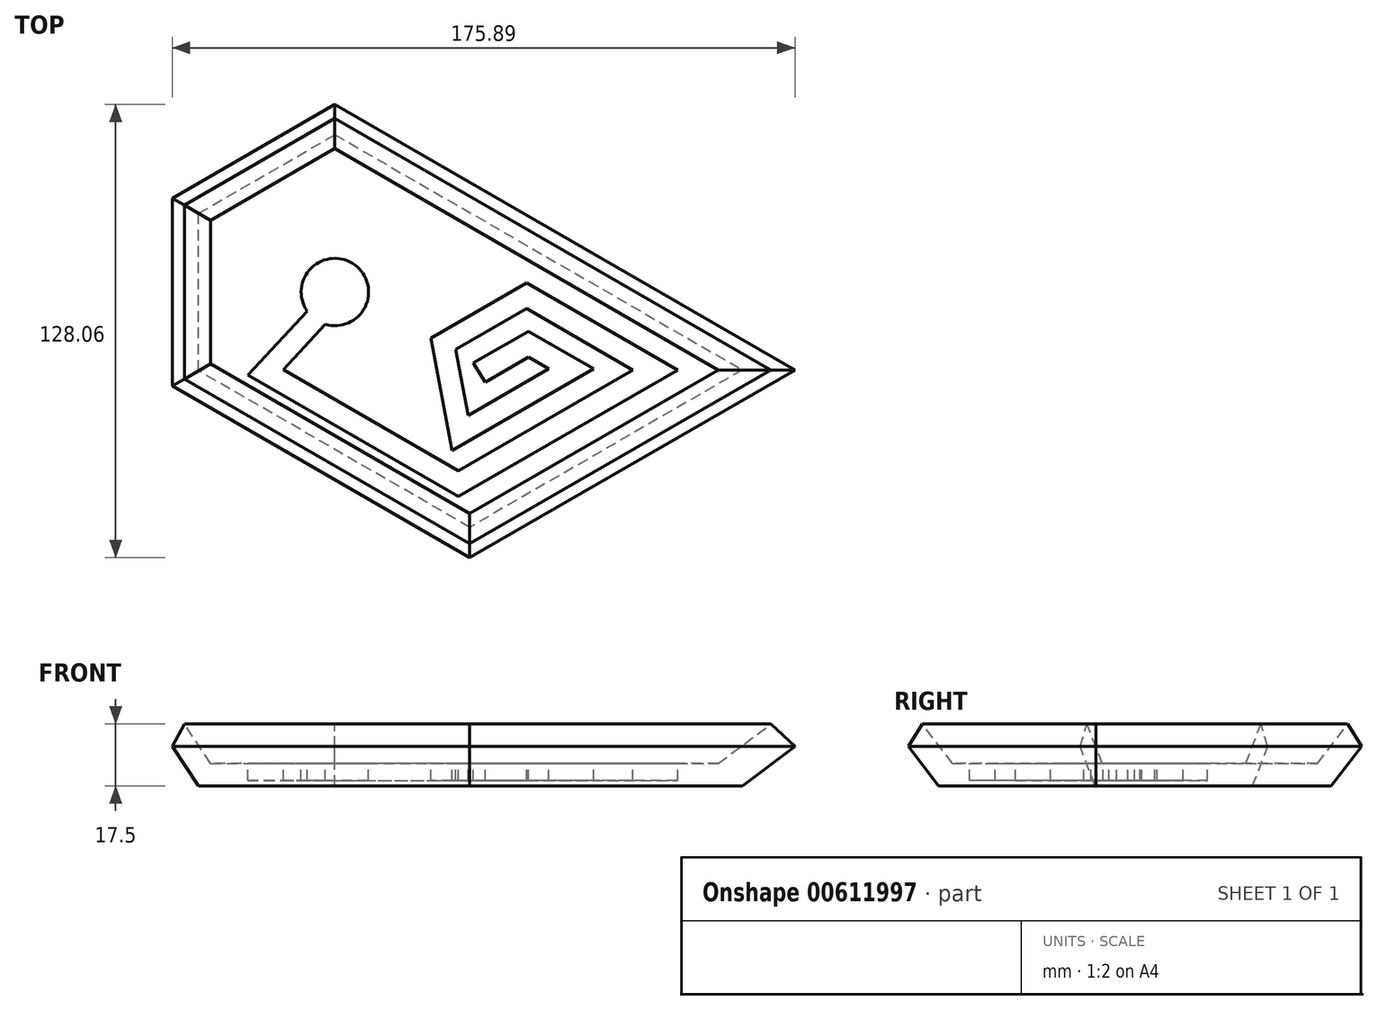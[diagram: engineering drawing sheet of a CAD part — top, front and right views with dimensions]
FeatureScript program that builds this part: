
annotation { "Feature Type Name" : "Feature", "Feature Type Description" : "" }
export const myFeature = defineFeature(function(context is Context, id is Id, definition is map)
    precondition{}
    {
        {
            var Q0;
            Q0=qCreatedBy(makeId("Top.planeOp"),FACE);
            var sketch = newSketch(context, id + "F0", { "sketchPlane" : qUnion([Q0])});
            skCircle(sketch, "E0.cCircle", {"center": v(0, 0) * mm, "radius": 38.5 * mm, "construction": true});
            skLineSegment(sketch, "E0.0", {"start": v(38.5, 22.22) * mm, "end": v(38.5, -22.22) * mm, "construction": true});
            skLineSegment(sketch, "E0.1", {"start": v(38.5, -22.23) * mm, "end": v(0, -44.45) * mm, "construction": true});
            skLineSegment(sketch, "E0.2", {"start": v(0, -44.45) * mm, "end": v(-38.5, -22.23) * mm});
            skLineSegment(sketch, "E0.3", {"start": v(-38.5, -22.22) * mm, "end": v(-38.5, 22.22) * mm});
            skLineSegment(sketch, "E0.4", {"start": v(-38.5, 22.22) * mm, "end": v(0, 44.45) * mm});
            skLineSegment(sketch, "E0.5", {"start": v(0, 44.45) * mm, "end": v(38.5, 22.23) * mm});
            skPoint(sketch, "E0.0.midPoint", {"position": v(38.5, 0) * mm});
            skLineSegment(sketch, "E1", {"start": v(38.5, 22.23) * mm, "end": v(115.09, -22) * mm});
            skLineSegment(sketch, "E2", {"start": v(115.09, -22) * mm, "end": v(38.1, -66.45) * mm});
            skLineSegment(sketch, "E3", {"start": v(38.1, -66.45) * mm, "end": v(0, -44.45) * mm});
            skSolve(sketch);
        }
        {
            var Q0;
            Q0=qCreatedBy(makeId("Top.planeOp"),FACE);
            cPlane(context, id + "F1", {"entities" : qUnion([Q0]), "cplaneType" : CPlaneType.OFFSET, "offset" : 19.05 * mm, "width" : 152.4 * mm, "height" : 152.4 * mm});
        }
        {
            var Q0;
            Q0=qCreatedBy(id+"F1.planeOp",FACE);
            var sketch = newSketch(context, id + "F2", { "sketchPlane" : qUnion([Q0])});
            skLineSegment(sketch, "E4.0", {"start": v(-51.2, -29.56) * mm, "end": v(-51.2, 29.56) * mm});
            skLineSegment(sketch, "E4.1", {"start": v(14.46, -67.46) * mm, "end": v(-51.2, -29.56) * mm});
            skLineSegment(sketch, "E4.2", {"start": v(-51.2, 29.56) * mm, "end": v(0, 59.11) * mm});
            skLineSegment(sketch, "E4.3", {"start": v(38.1, -81.11) * mm, "end": v(14.46, -67.46) * mm});
            skLineSegment(sketch, "E4.4", {"start": v(140.49, -22) * mm, "end": v(38.1, -81.11) * mm});
            skLineSegment(sketch, "E4.5", {"start": v(0, 59.11) * mm, "end": v(65.65, 21.2) * mm});
            skLineSegment(sketch, "E4.8", {"start": v(65.65, 21.2) * mm, "end": v(140.49, -22) * mm});
            skSolve(sketch);
        }
        {
            var Q0;
            Q0=makeQuery(id+"F0.imprint","IMPRINT",FACE,{"disambiguationData":[TD([[makeQuery(id+"F0.imprint","IMPRINT",EDGE,{"derivedFrom":sQuery(id+"F0.wireOp",EDGE,"E0.2")}),-1.0]])]});
            var Q1;
            Q1=makeQuery(id+"F2.imprint","IMPRINT",FACE,{"disambiguationData":[TD([[makeQuery(id+"F2.imprint","IMPRINT",EDGE,{"derivedFrom":sQuery(id+"F2.wireOp",EDGE,"E4.0")}),-1.0]])]});
            loft(context, id + "F3", {"sheetProfilesArray" : [{ "sheetProfileEntities" : qUnion([Q0]) }, { "sheetProfileEntities" : qUnion([Q1]) }]});
        }
        {
            var Q0;
            Q0=makeQuery(id+"F3.opLoft","CAP_FACE",FACE,{"disambiguationData":[OSD([makeQuery(id+"F2.imprint","IMPRINT",FACE,{"disambiguationData":[TD([[makeQuery(id+"F2.imprint","IMPRINT",EDGE,{"derivedFrom":sQuery(id+"F2.wireOp",EDGE,"E4.0")}),-1.0]])]})])],"isStart":true});
            shell(context, id + "F4", {"entities" : qUnion([Q0]), "thickness" : 6.35 * mm});
        }
        {
            var Q0;
            Q0=makeQuery(id+"F4.opShell","OFFSET_FACE",FACE,{"disambiguationData":[OSD([makeQuery(id+"F0.imprint","IMPRINT",FACE,{"disambiguationData":[TD([[makeQuery(id+"F0.imprint","IMPRINT",EDGE,{"derivedFrom":sQuery(id+"F0.wireOp",EDGE,"E0.2")}),-1.0]])]})])]});
            var sketch = newSketch(context, id + "F5", { "sketchPlane" : qUnion([Q0])});
            skCircle(sketch, "E5", {"center": v(0, 0) * mm, "radius": 9.53 * mm});
            skSolve(sketch);
        }
        {
            var Q0;
            Q0 = qSketchRegion(id + "F5", true);
            extrude(context, id + "F6", {"entities" : qUnion([Q0]), "operationType" : NewBodyOperationType.REMOVE, "oppositeDirection" : true, "depth" : 4.76 * mm, "offsetDistance" : 25.4 * mm});
        }
        {
            var Q0;
            Q0=makeQuery(id+"F4.opShell","OFFSET_FACE",FACE,{"disambiguationData":[OSD([makeQuery(id+"F0.imprint","IMPRINT",FACE,{"disambiguationData":[TD([[makeQuery(id+"F0.imprint","IMPRINT",EDGE,{"derivedFrom":sQuery(id+"F0.wireOp",EDGE,"E0.2")}),-1.0]])]})])]});
            var sketch = newSketch(context, id + "F7", { "sketchPlane" : qUnion([Q0])});
            skLineSegment(sketch, "E6", {"start": v(34.83, -50.45) * mm, "end": v(84.1, -22) * mm});
            skLineSegment(sketch, "E7", {"start": v(84.1, -22) * mm, "end": v(54.17, -4.71) * mm});
            skLineSegment(sketch, "E8", {"start": v(54.17, -4.71) * mm, "end": v(34.17, -16.26) * mm});
            skLineSegment(sketch, "E9", {"start": v(34.17, -16.26) * mm, "end": v(37.68, -34.83) * mm});
            skLineSegment(sketch, "E10", {"start": v(37.68, -34.83) * mm, "end": v(60.37, -21.73) * mm});
            skLineSegment(sketch, "E11", {"start": v(60.37, -21.73) * mm, "end": v(54.62, -18.42) * mm});
            skLineSegment(sketch, "E12", {"start": v(54.62, -18.42) * mm, "end": v(42.43, -25.46) * mm});
            skLineSegment(sketch, "E13.0", {"start": v(54.62, -11.08) * mm, "end": v(39.1, -20.05) * mm});
            skLineSegment(sketch, "E13.1", {"start": v(73.07, -21.73) * mm, "end": v(54.62, -11.08) * mm});
            skLineSegment(sketch, "E13.2", {"start": v(33.1, -44.8) * mm, "end": v(73.07, -21.73) * mm});
            skLineSegment(sketch, "E13.3", {"start": v(27.1, -13.01) * mm, "end": v(33.1, -44.8) * mm});
            skLineSegment(sketch, "E13.5", {"start": v(34.83, -57.78) * mm, "end": v(96.8, -22) * mm});
            skLineSegment(sketch, "E13.6", {"start": v(96.8, -22) * mm, "end": v(54.17, 2.62) * mm});
            skLineSegment(sketch, "E13.7", {"start": v(54.17, 2.62) * mm, "end": v(27.1, -13.01) * mm});
            skLineSegment(sketch, "E14", {"start": v(39.1, -20.05) * mm, "end": v(42.43, -25.46) * mm});
            skLineSegment(sketch, "E15", {"start": v(96.8, -22) * mm, "end": v(102.55, -18.68) * mm, "construction": true});
            skLineSegment(sketch, "E16", {"start": v(96.8, -22) * mm, "end": v(102.55, -25.31) * mm, "construction": true});
            skLineSegment(sketch, "E17", {"start": v(73.07, -21.73) * mm, "end": v(78.81, -25.05) * mm, "construction": true});
            skLineSegment(sketch, "E18", {"start": v(54.62, -11.08) * mm, "end": v(48.88, -7.77) * mm, "construction": true});
            skLineSegment(sketch, "E19", {"start": v(34.83, -57.78) * mm, "end": v(-24.61, -23.46) * mm});
            skLineSegment(sketch, "E20", {"start": v(-24.61, -23.46) * mm, "end": v(-7.87, -5.37) * mm});
            skLineSegment(sketch, "E21", {"start": v(34.83, -50.45) * mm, "end": v(-14.55, -21.94) * mm});
            skLineSegment(sketch, "E22", {"start": v(-14.55, -21.94) * mm, "end": v(-2.7, -9.13) * mm});
            skLineSegment(sketch, "E23", {"start": v(-2.7, -9.13) * mm, "end": v(-7.87, -5.37) * mm});
            skSolve(sketch);
        }
        {
            var Q0;
            Q0 = qSketchRegion(id + "F7", true);
            var Q1;
            Q1=makeQuery(id+"F6.boolean.opBoolean","COPY",FACE,{"derivedFrom":makeQuery(id+"F6.opExtrude","CAP_FACE",FACE,{"disambiguationData":[OSD([sQuery(id+"F5.wireOp",EDGE,"E5")])],"isStart":false})});
            extrude(context, id + "F8", {"entities" : qUnion([Q0]), "operationType" : NewBodyOperationType.REMOVE, "endBound" : BoundingType.UP_TO_SURFACE, "oppositeDirection" : true, "depth" : 25.4 * mm, "endBoundEntityFace" : qUnion([Q1]), "offsetDistance" : 25.4 * mm});
        }
        {
            var Q0;
            Q0=makeQuery(id+"F3.opLoft","MID_CAP_EDGE",EDGE,{"disambiguationData":[OSD([sQuery(id+"F2.wireOp",EDGE,"E4.0"),sQuery(id+"F2.wireOp",EDGE,"E4.1"),sQuery(id+"F2.wireOp",EDGE,"E4.3")])],"capPos":1.0});
            var Q1;
            Q1=makeQuery(id+"F3.opLoft","MID_CAP_EDGE",EDGE,{"disambiguationData":[OSD([sQuery(id+"F2.wireOp",EDGE,"E4.3"),sQuery(id+"F2.wireOp",EDGE,"E4.4"),sQuery(id+"F2.wireOp",EDGE,"E4.8")])],"capPos":1.0});
            var Q2;
            Q2=makeQuery(id+"F3.opLoft","MID_CAP_EDGE",EDGE,{"disambiguationData":[OSD([sQuery(id+"F2.wireOp",EDGE,"E4.4"),sQuery(id+"F2.wireOp",EDGE,"E4.5"),sQuery(id+"F2.wireOp",EDGE,"E4.8")])],"capPos":1.0});
            var Q3;
            Q3=makeQuery(id+"F3.opLoft","MID_CAP_EDGE",EDGE,{"disambiguationData":[OSD([sQuery(id+"F2.wireOp",EDGE,"E4.0"),sQuery(id+"F2.wireOp",EDGE,"E4.2"),sQuery(id+"F2.wireOp",EDGE,"E4.5")])],"capPos":1.0});
            var Q4;
            Q4=makeQuery(id+"F3.opLoft","MID_CAP_EDGE",EDGE,{"disambiguationData":[OSD([sQuery(id+"F2.wireOp",EDGE,"E4.0"),sQuery(id+"F2.wireOp",EDGE,"E4.1"),sQuery(id+"F2.wireOp",EDGE,"E4.2")])],"capPos":1.0});
            chamfer(context, id + "F9", {"entities" : qUnion([Q0, Q1, Q2, Q3, Q4]), "width" : 5.08 * mm, "tangentPropagation" : true});
        }
    });
